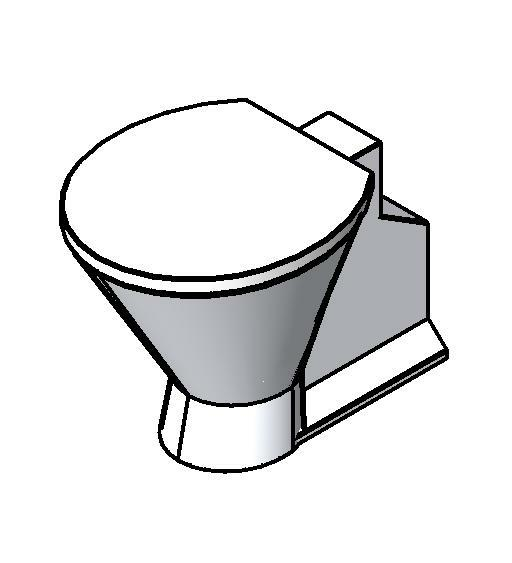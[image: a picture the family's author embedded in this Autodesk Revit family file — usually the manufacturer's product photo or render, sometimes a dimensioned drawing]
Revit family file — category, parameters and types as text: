
# Revit family: Deca_Cuba sobrepor quadrada 40cm_Cuba Slim_L.21040
name_source: partatom
category: Plumbing Fixtures
units: mm (PartAtom-declared; Revit-internal decimal feet)

## family parameters
Cut with Voids When Loaded = No
Host = Face
Part Type = Normal
Room Calculation Point = No
Round Connector Dimension = Use Radius
Shared = No

## types (5) — shared parameters
Acompanha o Produto = Acabamento da válvula cerâmica/Smartblock
Aprovado por = quattroD
Atendimento ao Cliente = 0800-0117073
Categoria = CUBAS
Composição Básica = Composição Básica: Argila / Feldispato / Caulim / Vidrados e corantes inorgânicos / Plásticos de Engenharia.
Composição Componente = PEBD
Cores Componente = transparente
Criado por = quattroD
Linha = CUBA SLIM
Manufacturer = DECA
Norma = NBR 16728-1 / NBR 16728-2
Peso Líquido (Kg) = 8.1
Pressão máx. funcionamento = 40mca
Pressão mín. funcionamento = 3mca
Saída de Esgoto = válvula curta
Segmento = LUXO
URL = www.deca.com.br
zero-valued in all types: CWFU, Default Elevation, Diâmetro Ponto de Esgoto, Diâmetro Água Fria, Raio Ponto de Esgoto, Raio Água Fria, WFU

## per-type parameters (varying)
| type | Cor Interna | Cor Principal | Código Pai | Informações Complementares | Material | Model |
| L.21040.17_Branco | Branco | Branco | L.21040.17 | Esmalte Protekto | Deca_Branco | L.21040.17 |
| L.21040.26_Barbante | Barbante | Barbante | L.21040.18 |  | Deca_Barbante | L.21040.26 |
| L.21040.49_Sálvia | Sálvia | Sálvia | L.21040.19 |  | Deca_Sálvia | L.21040.49 |
| L.21040.85_Cinza Antracite | Cinza Soft Antracite | Antracite | L.21040.20 |  | Deca_Cinza Antracite | L.21040.85 |
| L.21040.94_Ébano Fosco | Ébano Fosco | Ébano Fosco | L.21040.21 |  | Deca_Ébano Fosco | L.21040.94 |

## geometry (parser evidence)
native form markers: Sweep x2
no freeform markers — native parametric forms only
